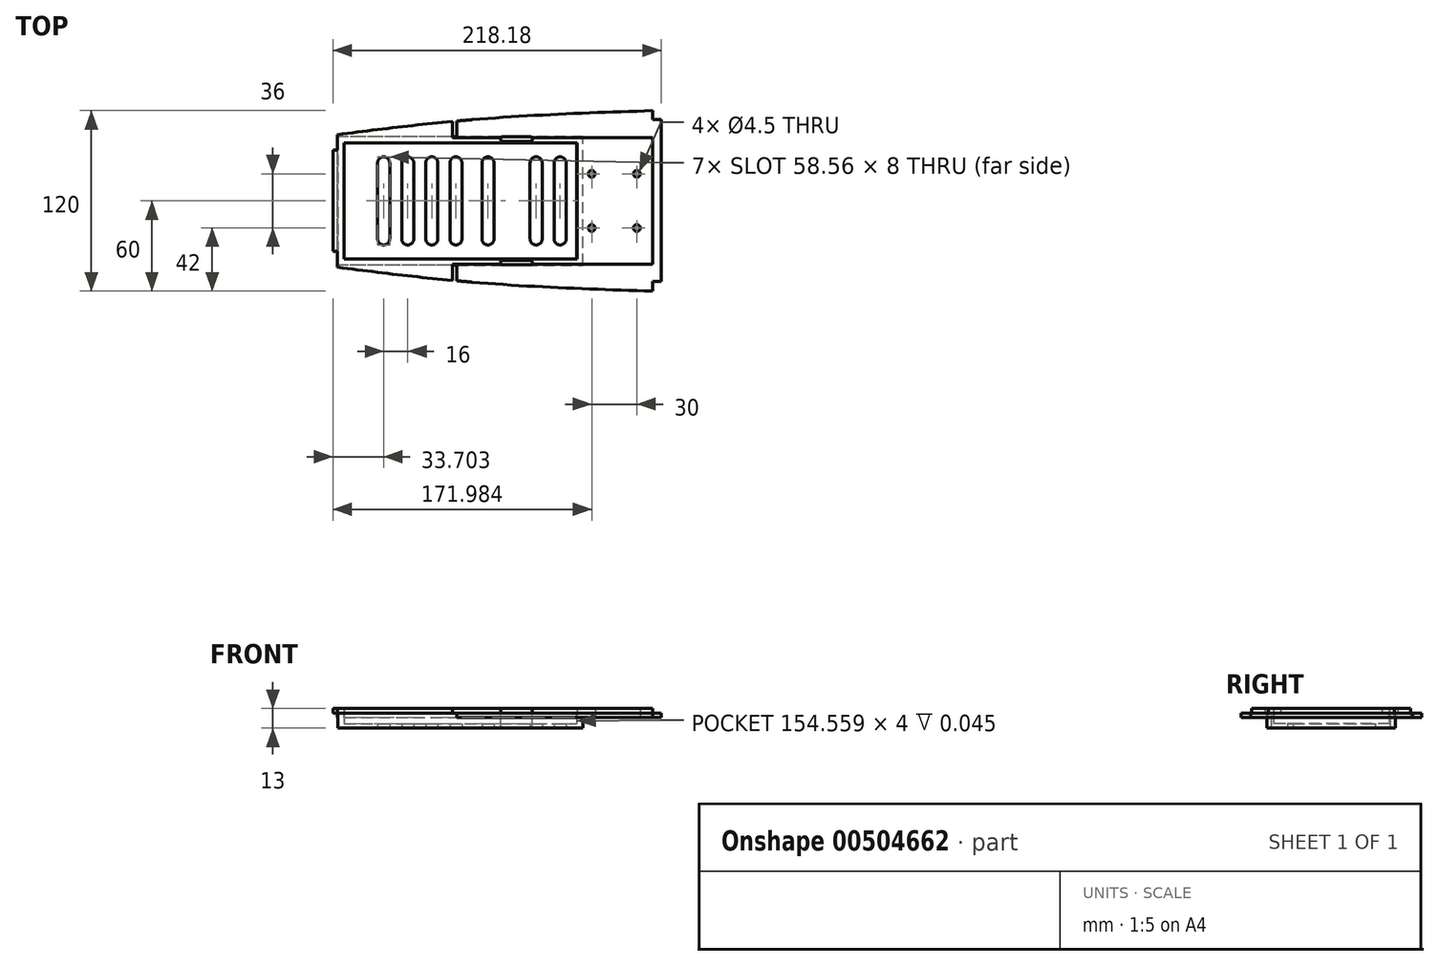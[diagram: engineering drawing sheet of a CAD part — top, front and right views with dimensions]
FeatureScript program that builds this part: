
annotation { "Feature Type Name" : "Feature", "Feature Type Description" : "" }
export const myFeature = defineFeature(function(context is Context, id is Id, definition is map)
    precondition{}
    {
        {
            var Q0;
            Q0=qCreatedBy(makeId("Top.planeOp"),FACE);
            var sketch = newSketch(context, id + "F0", { "sketchPlane" : qUnion([Q0])});
            skLineSegment(sketch, "E0.left", {"start": v(120, -40) * mm, "end": v(120, 40) * mm});
            skPoint(sketch, "E0.middle", {"position": v(0, 0) * mm});
            skLineSegment(sketch, "E1", {"start": v(0, 0) * mm, "end": v(0, 54) * mm});
            skPoint(sketch, "E1.endSnap0", {"position": v(0, 40) * mm});
            skLineSegment(sketch, "E2", {"start": v(120, 0) * mm, "end": v(120, 60) * mm});
            skLineSegment(sketch, "E3.MirrorCS", {"start": v(0, 0) * mm, "end": v(0, -54) * mm});
            skLineSegment(sketch, "E4.MirrorCS", {"start": v(120, 0) * mm, "end": v(120, -60) * mm});
            skFitSpline(sketch, "E5", {"points": [v(120, -60) * mm, v(0, -54) * mm, v(-120, -40) * mm], "startDerivative": vector(-240.5, 8.04) * mm, "endDerivative": vector(-239.5, 31.95) * mm});
            skFitSpline(sketch, "E6.MirrorCS", {"points": [v(120, 60) * mm, v(0, 54) * mm, v(-120, 40) * mm], "startDerivative": vector(-240.5, -8.04) * mm, "endDerivative": vector(-239.5, -31.95) * mm});
            skLineSegment(sketch, "E7.bottom", {"start": v(-85, -38.5) * mm, "end": v(70, -38.5) * mm});
            skLineSegment(sketch, "E7.top", {"start": v(-85, 38.5) * mm, "end": v(70, 38.5) * mm});
            skLineSegment(sketch, "E7.left", {"start": v(-85, -38.5) * mm, "end": v(-85, 38.5) * mm});
            skLineSegment(sketch, "E7.right", {"start": v(70, -38.5) * mm, "end": v(70, 38.5) * mm});
            skLineSegment(sketch, "E8", {"start": v(120, 0) * mm, "end": v(120, -42) * mm});
            skLineSegment(sketch, "E9", {"start": v(120, -42) * mm, "end": v(0, -42) * mm});
            skLineSegment(sketch, "E10.MirrorCS", {"start": v(120, 42) * mm, "end": v(0, 42) * mm});
            skLineSegment(sketch, "E11", {"start": v(-92.36, 43.66) * mm, "end": v(-92.36, -43.66) * mm});
            skPoint(sketch, "E12.start.orphan", {"position": v(70, 0) * mm});
            skLineSegment(sketch, "E13", {"start": v(-13, 52.85) * mm, "end": v(-13, 42) * mm});
            skLineSegment(sketch, "E14", {"start": v(-13, 42) * mm, "end": v(-10, 42) * mm});
            skLineSegment(sketch, "E15", {"start": v(-10, 42) * mm, "end": v(-10, 53.13) * mm});
            skLineSegment(sketch, "E16.MirrorCS", {"start": v(-10, -42) * mm, "end": v(-10, -53.13) * mm});
            skLineSegment(sketch, "E17.MirrorCS", {"start": v(-13, -52.85) * mm, "end": v(-13, -42) * mm});
            skLineSegment(sketch, "E18.MirrorCS", {"start": v(-13, -42) * mm, "end": v(-10, -42) * mm});
            skLineSegment(sketch, "E19.bottom", {"start": v(109.62, 18) * mm, "end": v(107.37, 18) * mm});
            skLineSegment(sketch, "E19.top", {"start": v(109.62, -18) * mm, "end": v(107.37, -18) * mm});
            skLineSegment(sketch, "E19.left", {"start": v(109.62, 18) * mm, "end": v(109.62, 15.75) * mm});
            skLineSegment(sketch, "E19.right", {"start": v(79.62, 18) * mm, "end": v(79.62, 15.75) * mm});
            skPoint(sketch, "E19.middle", {"position": v(94.62, 0) * mm});
            skCircle(sketch, "E20", {"center": v(79.62, 18) * mm, "radius": 2.25 * mm});
            skCircle(sketch, "E21", {"center": v(109.62, 18) * mm, "radius": 2.25 * mm});
            skCircle(sketch, "E22.MirrorC", {"center": v(79.62, -18) * mm, "radius": 2.25 * mm});
            skCircle(sketch, "E23.MirrorC", {"center": v(109.62, -18) * mm, "radius": 2.25 * mm});
            skLineSegment(sketch, "E24.trimOffspring", {"start": v(109.62, -15.75) * mm, "end": v(109.62, -18) * mm});
            skLineSegment(sketch, "E25.trimOffspring", {"start": v(81.87, 18) * mm, "end": v(79.62, 18) * mm});
            skLineSegment(sketch, "E26.trimOffspring", {"start": v(79.62, -15.75) * mm, "end": v(79.62, -18) * mm});
            skLineSegment(sketch, "E27.trimOffspring", {"start": v(81.87, -18) * mm, "end": v(79.62, -18) * mm});
            skLineSegment(sketch, "E28.bottom", {"start": v(120, 54.1) * mm, "end": v(125.82, 54.1) * mm});
            skLineSegment(sketch, "E28.top", {"start": v(120, -53.5) * mm, "end": v(125.82, -53.5) * mm});
            skLineSegment(sketch, "E28.left", {"start": v(120, 54.1) * mm, "end": v(120, -53.5) * mm});
            skLineSegment(sketch, "E28.right", {"start": v(125.82, 54.1) * mm, "end": v(125.82, -53.5) * mm});
            skLineSegment(sketch, "E29", {"start": v(-92.36, 43.66) * mm, "end": v(-92.36, 33.66) * mm});
            skLineSegment(sketch, "E30", {"start": v(-92.36, 33.66) * mm, "end": v(-89.36, 33.66) * mm});
            skLineSegment(sketch, "E31", {"start": v(-89.36, 33.66) * mm, "end": v(-89.36, 44.05) * mm});
            skLineSegment(sketch, "E32.MirrorCS", {"start": v(-89.36, -33.66) * mm, "end": v(-89.36, -44.05) * mm});
            skLineSegment(sketch, "E33.MirrorCS", {"start": v(-92.36, -33.66) * mm, "end": v(-89.36, -33.66) * mm});
            skLineSegment(sketch, "E34", {"start": v(0, 42) * mm, "end": v(-89.36, 42) * mm});
            skLineSegment(sketch, "E35", {"start": v(-89.36, 42) * mm, "end": v(-89.36, -42) * mm});
            skLineSegment(sketch, "E36", {"start": v(-89.36, -42) * mm, "end": v(0, -42) * mm});
            skLineSegment(sketch, "E37", {"start": v(70, 38.5) * mm, "end": v(120, 38.5) * mm});
            skLineSegment(sketch, "E38", {"start": v(70, -38.5) * mm, "end": v(120, -38.5) * mm});
            skLineSegment(sketch, "E39", {"start": v(115.27, 38.5) * mm, "end": v(115.27, -38.5) * mm});
            skSolve(sketch);
        }
        {
            var Q0;
            {var subQ8=sQuery(id+"F0.wireOp",EDGE,"E7.right");Q0=makeQuery(id+"F0.imprint","IMPRINT",FACE,{"disambiguationData":[TD([[makeQuery(id+"F0.imprint","IMPRINT",EDGE,{"derivedFrom":subQ8}),-1.0]])]});}
            var Q1;
            {var subQ7=sQuery(id+"F0.wireOp",EDGE,"E7.left");Q1=makeQuery(id+"F0.imprint","IMPRINT",FACE,{"disambiguationData":[TD([[makeQuery(id+"F0.imprint","IMPRINT",EDGE,{"derivedFrom":subQ7}),1.0]])]});}
            var Q2;
            {var subQ0=sQuery(id+"F0.wireOp",EDGE,"E30");Q2=makeQuery(id+"F0.imprint","IMPRINT",FACE,{"disambiguationData":[TD([[makeQuery(id+"F0.imprint","IMPRINT",EDGE,{"derivedFrom":subQ0}),-1.0]])]});}
            var Q3;
            {var subQ0=sQuery(id+"F0.wireOp",EDGE,"E10.MirrorCS");Q3=makeQuery(id+"F0.imprint","IMPRINT",FACE,{"disambiguationData":[TD([[makeQuery(id+"F0.imprint","IMPRINT",EDGE,{"derivedFrom":subQ0}),1.0]])]});}
            var Q4;
            {var subQ0=sQuery(id+"F0.wireOp",EDGE,"E9");Q4=makeQuery(id+"F0.imprint","IMPRINT",FACE,{"disambiguationData":[TD([[makeQuery(id+"F0.imprint","IMPRINT",EDGE,{"derivedFrom":subQ0}),-1.0]])]});}
            var Q5;
            {var subQ3=sQuery(id+"F0.wireOp",EDGE,"E39");Q5=makeQuery(id+"F0.imprint","IMPRINT",FACE,{"disambiguationData":[TD([[makeQuery(id+"F0.imprint","IMPRINT",EDGE,{"derivedFrom":subQ3}),1.0]])]});}
            var Q6;
            {var subQ0=sQuery(id+"F0.wireOp",EDGE,"E13");Q6=makeQuery(id+"F0.imprint","IMPRINT",FACE,{"disambiguationData":[TD([[makeQuery(id+"F0.imprint","IMPRINT",EDGE,{"derivedFrom":subQ0}),-1.0]])]});}
            var Q7;
            {var subQ0=sQuery(id+"F0.wireOp",EDGE,"E17.MirrorCS");Q7=makeQuery(id+"F0.imprint","IMPRINT",FACE,{"disambiguationData":[TD([[makeQuery(id+"F0.imprint","IMPRINT",EDGE,{"derivedFrom":subQ0}),1.0]])]});}
            extrude(context, id + "F1", {"entities" : qUnion([Q0, Q1, Q2, Q3, Q4, Q5, Q6, Q7]), "depth" : 3 * mm});
        }
        {
            var Q0;
            {var subQ2=sQuery(id+"F0.wireOp",EDGE,"E4.MirrorCS");Q0=makeQuery(id+"F0.imprint","IMPRINT",FACE,{"disambiguationData":[TD([[makeQuery(id+"F0.imprint","IMPRINT",EDGE,{"derivedFrom":subQ2}),-1.0]])]});}
            var Q1;
            {var subQ0=sQuery(id+"F0.wireOp",EDGE,"E9");Q1=makeQuery(id+"F0.imprint","IMPRINT",FACE,{"disambiguationData":[TD([[makeQuery(id+"F0.imprint","IMPRINT",EDGE,{"derivedFrom":subQ0}),-1.0]])]});}
            var Q2;
            {var subQ3=sQuery(id+"F0.wireOp",EDGE,"E39");Q2=makeQuery(id+"F0.imprint","IMPRINT",FACE,{"disambiguationData":[TD([[makeQuery(id+"F0.imprint","IMPRINT",EDGE,{"derivedFrom":subQ3}),1.0]])]});}
            var Q3;
            {var subQ0=sQuery(id+"F0.wireOp",EDGE,"E10.MirrorCS");Q3=makeQuery(id+"F0.imprint","IMPRINT",FACE,{"disambiguationData":[TD([[makeQuery(id+"F0.imprint","IMPRINT",EDGE,{"derivedFrom":subQ0}),1.0]])]});}
            var Q4;
            {var subQ1=sQuery(id+"F0.wireOp",EDGE,"E2");Q4=makeQuery(id+"F0.imprint","IMPRINT",FACE,{"disambiguationData":[TD([[makeQuery(id+"F0.imprint","IMPRINT",EDGE,{"derivedFrom":subQ1}),1.0]])]});}
            var Q5;
            {var subQ3=sQuery(id+"F0.wireOp",EDGE,"E7.left");Q5=makeQuery(id+"F0.imprint","IMPRINT",FACE,{"disambiguationData":[TD([[makeQuery(id+"F0.imprint","IMPRINT",EDGE,{"derivedFrom":subQ3}),1.0]])]});}
            var Q6;
            {var subQ8=sQuery(id+"F0.wireOp",EDGE,"E28.bottom");Q6=makeQuery(id+"F0.imprint","IMPRINT",FACE,{"disambiguationData":[TD([[makeQuery(id+"F0.imprint","IMPRINT",EDGE,{"derivedFrom":subQ8}),-1.0]])]});}
            var Q7;
            {var subQ5=sQuery(id+"F0.wireOp",EDGE,"E16.MirrorCS");Q7=makeQuery(id+"F0.imprint","IMPRINT",FACE,{"disambiguationData":[TD([[makeQuery(id+"F0.imprint","IMPRINT",EDGE,{"derivedFrom":subQ5}),1.0]])]});}
            var Q8;
            {var subQ5=sQuery(id+"F0.wireOp",EDGE,"E15");Q8=makeQuery(id+"F0.imprint","IMPRINT",FACE,{"disambiguationData":[TD([[makeQuery(id+"F0.imprint","IMPRINT",EDGE,{"derivedFrom":subQ5}),-1.0]])]});}
            var Q9;
            {var subQ7=sQuery(id+"F0.wireOp",EDGE,"E7.right");Q9=makeQuery(id+"F0.imprint","IMPRINT",FACE,{"disambiguationData":[TD([[makeQuery(id+"F0.imprint","IMPRINT",EDGE,{"derivedFrom":subQ7}),-1.0]])]});}
            extrude(context, id + "F2", {"entities" : qUnion([Q0, Q1, Q2, Q3, Q4, Q5, Q6, Q7, Q8, Q9]), "operationType" : NewBodyOperationType.ADD, "oppositeDirection" : true, "depth" : 3 * mm});
        }
        {
            var Q0;
            Q0=qCreatedBy(makeId("Top.planeOp"),FACE);
            cPlane(context, id + "F3", {"entities" : qUnion([Q0]), "cplaneType" : CPlaneType.OFFSET, "offset" : 10 * mm, "oppositeDirection" : true, "width" : 150 * mm, "height" : 150 * mm});
        }
        {
            var Q0;
            Q0=qCreatedBy(id+"F3.planeOp",FACE);
            var sketch = newSketch(context, id + "F4", { "sketchPlane" : qUnion([Q0])});
            skLineSegment(sketch, "E40.bottom", {"start": v(69.63, -38.46) * mm, "end": v(-84.93, -38.46) * mm});
            skLineSegment(sketch, "E40.top", {"start": v(69.63, 38.54) * mm, "end": v(-84.93, 38.54) * mm});
            skLineSegment(sketch, "E40.left", {"start": v(69.63, -38.46) * mm, "end": v(69.63, 38.54) * mm});
            skLineSegment(sketch, "E40.right", {"start": v(-84.93, -38.46) * mm, "end": v(-84.93, 38.54) * mm});
            skLineSegment(sketch, "E41.0", {"start": v(73.83, -42.66) * mm, "end": v(-89.13, -42.66) * mm});
            skLineSegment(sketch, "E41.1", {"start": v(73.83, -42.66) * mm, "end": v(73.83, 42.74) * mm});
            skLineSegment(sketch, "E41.2", {"start": v(73.83, 42.74) * mm, "end": v(-89.13, 42.74) * mm});
            skLineSegment(sketch, "E41.3", {"start": v(-89.13, -42.66) * mm, "end": v(-89.13, 42.74) * mm});
            skArc(sketch, "E42", {"start": v(54.66, -25.28) * mm, "mid": v(58.66, -29.28) * mm, "end": v(62.66, -25.28) * mm});
            skArc(sketch, "E43", {"start": v(38.66, -25.28) * mm, "mid": v(42.66, -29.28) * mm, "end": v(46.66, -25.28) * mm});
            skArc(sketch, "E44", {"start": v(22.66, -25.18) * mm, "mid": v(26.6, -29.28) * mm, "end": v(30.66, -25.28) * mm});
            skArc(sketch, "E45", {"start": v(6.66, -25.28) * mm, "mid": v(10.66, -29.28) * mm, "end": v(14.66, -25.28) * mm});
            skArc(sketch, "E46.MirrorC", {"start": v(54.66, 25.28) * mm, "mid": v(58.66, 29.28) * mm, "end": v(62.66, 25.28) * mm});
            skArc(sketch, "E47.MirrorC", {"start": v(38.66, 25.28) * mm, "mid": v(42.66, 29.28) * mm, "end": v(46.66, 25.28) * mm});
            skArc(sketch, "E48.MirrorC", {"start": v(22.66, 25.28) * mm, "mid": v(26.66, 29.28) * mm, "end": v(30.66, 25.28) * mm});
            skArc(sketch, "E49.MirrorC", {"start": v(6.66, 25.28) * mm, "mid": v(10.66, 29.28) * mm, "end": v(14.66, 25.28) * mm});
            skLineSegment(sketch, "E50", {"start": v(62.66, -25.28) * mm, "end": v(62.66, 25.28) * mm});
            skLineSegment(sketch, "E51", {"start": v(54.66, -25.28) * mm, "end": v(54.66, 25.28) * mm});
            skLineSegment(sketch, "E52", {"start": v(46.66, -25.28) * mm, "end": v(46.66, 25.28) * mm});
            skLineSegment(sketch, "E53", {"start": v(38.66, -25.28) * mm, "end": v(38.66, 25.28) * mm});
            skLineSegment(sketch, "E54", {"start": v(30.66, -25.28) * mm, "end": v(30.66, 25.28) * mm});
            skLineSegment(sketch, "E55", {"start": v(22.66, -25.18) * mm, "end": v(22.66, 25.28) * mm});
            skLineSegment(sketch, "E56", {"start": v(14.66, -25.28) * mm, "end": v(14.66, 25.28) * mm});
            skLineSegment(sketch, "E57", {"start": v(6.66, -25.28) * mm, "end": v(6.66, 25.28) * mm});
            skLineSegment(sketch, "E58.MirrorCS", {"start": v(-6.66, -25.28) * mm, "end": v(-6.66, 25.28) * mm});
            skArc(sketch, "E59.MirrorCS", {"start": v(-6.66, -25.28) * mm, "mid": v(-10.66, -29.28) * mm, "end": v(-14.66, -25.28) * mm});
            skLineSegment(sketch, "E60.MirrorCS", {"start": v(-14.66, -25.28) * mm, "end": v(-14.66, 25.28) * mm});
            skArc(sketch, "E61.MirrorCS", {"start": v(-6.66, 25.28) * mm, "mid": v(-10.66, 29.28) * mm, "end": v(-14.66, 25.28) * mm});
            skLineSegment(sketch, "E62.MirrorCS", {"start": v(-22.66, -25.18) * mm, "end": v(-22.66, 25.28) * mm});
            skArc(sketch, "E63.MirrorCS", {"start": v(-22.66, -25.18) * mm, "mid": v(-26.6, -29.28) * mm, "end": v(-30.66, -25.28) * mm});
            skLineSegment(sketch, "E64.MirrorCS", {"start": v(-30.66, -25.28) * mm, "end": v(-30.66, 25.28) * mm});
            skArc(sketch, "E65.MirrorCS", {"start": v(-22.66, 25.28) * mm, "mid": v(-26.66, 29.28) * mm, "end": v(-30.66, 25.28) * mm});
            skLineSegment(sketch, "E66.MirrorCS", {"start": v(-38.66, -25.28) * mm, "end": v(-38.66, 25.28) * mm});
            skArc(sketch, "E67.MirrorCS", {"start": v(-38.66, -25.28) * mm, "mid": v(-42.66, -29.28) * mm, "end": v(-46.66, -25.28) * mm});
            skLineSegment(sketch, "E68.MirrorCS", {"start": v(-46.66, -25.28) * mm, "end": v(-46.66, 25.28) * mm});
            skArc(sketch, "E69.MirrorCS", {"start": v(-38.66, 25.28) * mm, "mid": v(-42.66, 29.28) * mm, "end": v(-46.66, 25.28) * mm});
            skLineSegment(sketch, "E70.MirrorCS", {"start": v(-54.66, -25.28) * mm, "end": v(-54.66, 25.28) * mm});
            skArc(sketch, "E71.MirrorCS", {"start": v(-54.66, -25.28) * mm, "mid": v(-58.66, -29.28) * mm, "end": v(-62.66, -25.28) * mm});
            skLineSegment(sketch, "E72.MirrorCS", {"start": v(-62.66, -25.28) * mm, "end": v(-62.66, 25.28) * mm});
            skArc(sketch, "E73.MirrorCS", {"start": v(-54.66, 25.28) * mm, "mid": v(-58.66, 29.28) * mm, "end": v(-62.66, 25.28) * mm});
            skSolve(sketch);
        }
        {
            var Q0;
            Q0=makeQuery(id+"F4.imprint","IMPRINT",FACE,{"disambiguationData":[TD([[makeQuery(id+"F4.imprint","IMPRINT",EDGE,{"derivedFrom":sQuery(id+"F4.wireOp",EDGE,"E40.bottom")}),-1.0]])]});
            var Q1;
            Q1=makeQuery(id+"F4.imprint","IMPRINT",FACE,{"disambiguationData":[TD([[makeQuery(id+"F4.imprint","IMPRINT",EDGE,{"derivedFrom":sQuery(id+"F4.wireOp",EDGE,"E40.bottom")}),1.0]])]});
            var Q2;
            Q2=makeQuery(id+"F4.imprint","IMPRINT",FACE,{"disambiguationData":[TD([[makeQuery(id+"F4.imprint","IMPRINT",EDGE,{"derivedFrom":sQuery(id+"F4.wireOp",EDGE,"E44")}),1.0]])]});
            extrude(context, id + "F5", {"entities" : qUnion([Q0, Q1, Q2]), "depth" : 3 * mm});
        }
        {
            var Q0;
            Q0=makeQuery(id+"F4.imprint","IMPRINT",FACE,{"disambiguationData":[TD([[makeQuery(id+"F4.imprint","IMPRINT",EDGE,{"derivedFrom":sQuery(id+"F4.wireOp",EDGE,"E40.bottom")}),1.0]])]});
            extrude(context, id + "F6", {"entities" : qUnion([Q0]), "operationType" : NewBodyOperationType.ADD, "depth" : 10 * mm});
        }
        {
            var Q0;
            Q0=makeQuery(id+"F1.opExtrude","CAP_FACE",FACE,{"disambiguationData":[OSD([sQuery(id+"F0.wireOp",EDGE,"E5"),sQuery(id+"F0.wireOp",EDGE,"E6.MirrorCS"),sQuery(id+"F0.wireOp",EDGE,"E7.bottom"),sQuery(id+"F0.wireOp",EDGE,"E7.top"),sQuery(id+"F0.wireOp",EDGE,"E7.left"),sQuery(id+"F0.wireOp",EDGE,"E7.right"),sQuery(id+"F0.wireOp",EDGE,"E9"),sQuery(id+"F0.wireOp",EDGE,"E10.MirrorCS"),sQuery(id+"F0.wireOp",EDGE,"E11"),sQuery(id+"F0.wireOp",EDGE,"E13"),sQuery(id+"F0.wireOp",EDGE,"E17.MirrorCS"),sQuery(id+"F0.wireOp",EDGE,"E20"),sQuery(id+"F0.wireOp",EDGE,"E21"),sQuery(id+"F0.wireOp",EDGE,"E22.MirrorC"),sQuery(id+"F0.wireOp",EDGE,"E23.MirrorC"),sQuery(id+"F0.wireOp",EDGE,"E28.left"),sQuery(id+"F0.wireOp",EDGE,"E30"),sQuery(id+"F0.wireOp",EDGE,"E31"),sQuery(id+"F0.wireOp",EDGE,"E32.MirrorCS"),sQuery(id+"F0.wireOp",EDGE,"E33.MirrorCS"),sQuery(id+"F0.wireOp",EDGE,"E34"),sQuery(id+"F0.wireOp",EDGE,"E35"),sQuery(id+"F0.wireOp",EDGE,"E36")])],"isStart":false});
            var sketch = newSketch(context, id + "F7", { "sketchPlane" : qUnion([Q0])});
            skLineSegment(sketch, "E74.bottom", {"start": v(20.1, 39.55) * mm, "end": v(39.1, 39.55) * mm});
            skLineSegment(sketch, "E74.top", {"start": v(20.1, 42.55) * mm, "end": v(39.1, 42.55) * mm});
            skLineSegment(sketch, "E74.left", {"start": v(19.1, 40.55) * mm, "end": v(19.1, 41.53) * mm});
            skLineSegment(sketch, "E74.right", {"start": v(40.1, 40.55) * mm, "end": v(40.1, 41.55) * mm});
            skPoint(sketch, "E75.visualSharp", {"position": v(19.1, 42.55) * mm});
            skArc(sketch, "E75.filletArc", {"start": v(20.1, 42.55) * mm, "mid": v(19.39, 42.25) * mm, "end": v(19.1, 41.53) * mm});
            skPoint(sketch, "E76.visualSharp", {"position": v(40.1, 42.55) * mm});
            skArc(sketch, "E76.filletArc", {"start": v(40.1, 41.55) * mm, "mid": v(39.8, 42.25) * mm, "end": v(39.1, 42.55) * mm});
            skPoint(sketch, "E77.visualSharp", {"position": v(40.1, 39.55) * mm});
            skArc(sketch, "E77.filletArc", {"start": v(39.1, 39.55) * mm, "mid": v(39.8, 39.84) * mm, "end": v(40.1, 40.55) * mm});
            skPoint(sketch, "E78.visualSharp", {"position": v(19.1, 39.55) * mm});
            skArc(sketch, "E78.filletArc", {"start": v(19.1, 40.55) * mm, "mid": v(19.39, 39.84) * mm, "end": v(20.1, 39.55) * mm});
            skLineSegment(sketch, "E79.MirrorCS", {"start": v(20.1, -39.55) * mm, "end": v(39.1, -39.55) * mm});
            skLineSegment(sketch, "E80.MirrorCS", {"start": v(20.1, -42.55) * mm, "end": v(39.1, -42.55) * mm});
            skArc(sketch, "E81.MirrorCS", {"start": v(40.1, -41.55) * mm, "mid": v(39.8, -42.25) * mm, "end": v(39.1, -42.55) * mm});
            skLineSegment(sketch, "E82.MirrorCS", {"start": v(40.1, -40.55) * mm, "end": v(40.1, -41.55) * mm});
            skPoint(sketch, "E83.MirrorP", {"position": v(40.1, -39.55) * mm});
            skArc(sketch, "E84.MirrorCS", {"start": v(39.1, -39.55) * mm, "mid": v(39.8, -39.84) * mm, "end": v(40.1, -40.55) * mm});
            skArc(sketch, "E85.MirrorCS", {"start": v(19.1, -40.55) * mm, "mid": v(19.39, -39.84) * mm, "end": v(20.1, -39.55) * mm});
            skLineSegment(sketch, "E86.MirrorCS", {"start": v(19.1, -40.55) * mm, "end": v(19.1, -41.53) * mm});
            skArc(sketch, "E87.MirrorCS", {"start": v(20.1, -42.55) * mm, "mid": v(19.39, -42.25) * mm, "end": v(19.1, -41.53) * mm});
            skSolve(sketch);
        }
        {
            var Q0;
            Q0=makeQuery(id+"F7.imprint","IMPRINT",FACE,{"disambiguationData":[TD([[makeQuery(id+"F7.imprint","IMPRINT",EDGE,{"derivedFrom":sQuery(id+"F7.wireOp",EDGE,"E74.bottom")}),1.0]])]});
            var Q1;
            Q1=makeQuery(id+"F7.imprint","IMPRINT",FACE,{"disambiguationData":[TD([[makeQuery(id+"F7.imprint","IMPRINT",EDGE,{"derivedFrom":sQuery(id+"F7.wireOp",EDGE,"E79.MirrorCS")}),-1.0]])]});
            var Q2;
            {var subQ0=sQuery(id+"F7.wireOp",EDGE,"E74.top");Q2=makeQuery(id+"F7.imprint","IMPRINT",FACE,{"disambiguationData":[TD([[makeQuery(id+"F7.imprint","IMPRINT",EDGE,{"derivedFrom":subQ0}),-1.0]])]});}
            var Q3;
            {var subQ0=sQuery(id+"F7.wireOp",EDGE,"E80.MirrorCS");Q3=makeQuery(id+"F7.imprint","IMPRINT",FACE,{"disambiguationData":[TD([[makeQuery(id+"F7.imprint","IMPRINT",EDGE,{"derivedFrom":subQ0}),1.0]])]});}
            extrude(context, id + "F8", {"entities" : qUnion([Q0, Q1, Q2, Q3]), "operationType" : NewBodyOperationType.REMOVE, "oppositeDirection" : true, "depth" : 25 * mm});
        }
        {
            var Q0;
            Q0=makeQuery(id+"F8.boolean.opBoolean","INTERSECT",EDGE,{"derivedFrom":[makeQuery(id+"F5.opExtrude","CAP_FACE",FACE,{"disambiguationData":[OSD([sQuery(id+"F4.wireOp",EDGE,"E41.0"),sQuery(id+"F4.wireOp",EDGE,"E41.1"),sQuery(id+"F4.wireOp",EDGE,"E41.2"),sQuery(id+"F4.wireOp",EDGE,"E41.3"),sQuery(id+"F4.wireOp",EDGE,"E42"),sQuery(id+"F4.wireOp",EDGE,"E43"),sQuery(id+"F4.wireOp",EDGE,"E45"),sQuery(id+"F4.wireOp",EDGE,"E46.MirrorC"),sQuery(id+"F4.wireOp",EDGE,"E47.MirrorC"),sQuery(id+"F4.wireOp",EDGE,"E49.MirrorC"),sQuery(id+"F4.wireOp",EDGE,"E50"),sQuery(id+"F4.wireOp",EDGE,"E51"),sQuery(id+"F4.wireOp",EDGE,"E52"),sQuery(id+"F4.wireOp",EDGE,"E53"),sQuery(id+"F4.wireOp",EDGE,"E56"),sQuery(id+"F4.wireOp",EDGE,"E57"),sQuery(id+"F4.wireOp",EDGE,"E58.MirrorCS"),sQuery(id+"F4.wireOp",EDGE,"E59.MirrorCS"),sQuery(id+"F4.wireOp",EDGE,"E60.MirrorCS"),sQuery(id+"F4.wireOp",EDGE,"E61.MirrorCS"),sQuery(id+"F4.wireOp",EDGE,"E62.MirrorCS"),sQuery(id+"F4.wireOp",EDGE,"E63.MirrorCS"),sQuery(id+"F4.wireOp",EDGE,"E64.MirrorCS"),sQuery(id+"F4.wireOp",EDGE,"E65.MirrorCS"),sQuery(id+"F4.wireOp",EDGE,"E66.MirrorCS"),sQuery(id+"F4.wireOp",EDGE,"E67.MirrorCS"),sQuery(id+"F4.wireOp",EDGE,"E68.MirrorCS"),sQuery(id+"F4.wireOp",EDGE,"E69.MirrorCS"),sQuery(id+"F4.wireOp",EDGE,"E70.MirrorCS"),sQuery(id+"F4.wireOp",EDGE,"E71.MirrorCS"),sQuery(id+"F4.wireOp",EDGE,"E72.MirrorCS"),sQuery(id+"F4.wireOp",EDGE,"E73.MirrorCS")])],"isStart":true}),makeQuery(id+"F8.opExtrude","SWEPT_FACE",FACE,{"disambiguationData":[OSD([sQuery(id+"F7.wireOp",EDGE,"E79.MirrorCS")])]})]});
            var Q1;
            Q1=makeQuery(id+"F8.boolean.opBoolean","INTERSECT",EDGE,{"derivedFrom":[makeQuery(id+"F5.opExtrude","CAP_FACE",FACE,{"disambiguationData":[OSD([sQuery(id+"F4.wireOp",EDGE,"E41.0"),sQuery(id+"F4.wireOp",EDGE,"E41.1"),sQuery(id+"F4.wireOp",EDGE,"E41.2"),sQuery(id+"F4.wireOp",EDGE,"E41.3"),sQuery(id+"F4.wireOp",EDGE,"E42"),sQuery(id+"F4.wireOp",EDGE,"E43"),sQuery(id+"F4.wireOp",EDGE,"E45"),sQuery(id+"F4.wireOp",EDGE,"E46.MirrorC"),sQuery(id+"F4.wireOp",EDGE,"E47.MirrorC"),sQuery(id+"F4.wireOp",EDGE,"E49.MirrorC"),sQuery(id+"F4.wireOp",EDGE,"E50"),sQuery(id+"F4.wireOp",EDGE,"E51"),sQuery(id+"F4.wireOp",EDGE,"E52"),sQuery(id+"F4.wireOp",EDGE,"E53"),sQuery(id+"F4.wireOp",EDGE,"E56"),sQuery(id+"F4.wireOp",EDGE,"E57"),sQuery(id+"F4.wireOp",EDGE,"E58.MirrorCS"),sQuery(id+"F4.wireOp",EDGE,"E59.MirrorCS"),sQuery(id+"F4.wireOp",EDGE,"E60.MirrorCS"),sQuery(id+"F4.wireOp",EDGE,"E61.MirrorCS"),sQuery(id+"F4.wireOp",EDGE,"E62.MirrorCS"),sQuery(id+"F4.wireOp",EDGE,"E63.MirrorCS"),sQuery(id+"F4.wireOp",EDGE,"E64.MirrorCS"),sQuery(id+"F4.wireOp",EDGE,"E65.MirrorCS"),sQuery(id+"F4.wireOp",EDGE,"E66.MirrorCS"),sQuery(id+"F4.wireOp",EDGE,"E67.MirrorCS"),sQuery(id+"F4.wireOp",EDGE,"E68.MirrorCS"),sQuery(id+"F4.wireOp",EDGE,"E69.MirrorCS"),sQuery(id+"F4.wireOp",EDGE,"E70.MirrorCS"),sQuery(id+"F4.wireOp",EDGE,"E71.MirrorCS"),sQuery(id+"F4.wireOp",EDGE,"E72.MirrorCS"),sQuery(id+"F4.wireOp",EDGE,"E73.MirrorCS")])],"isStart":true}),makeQuery(id+"F8.opExtrude","SWEPT_FACE",FACE,{"disambiguationData":[OSD([sQuery(id+"F7.wireOp",EDGE,"E74.bottom")])]})]});
            fillet(context, id + "F9", {"entities" : qUnion([Q0, Q1]), "radius" : 1 * mm, "tangentPropagation" : true, "allowEdgeOverflow" : false});
        }
    });
